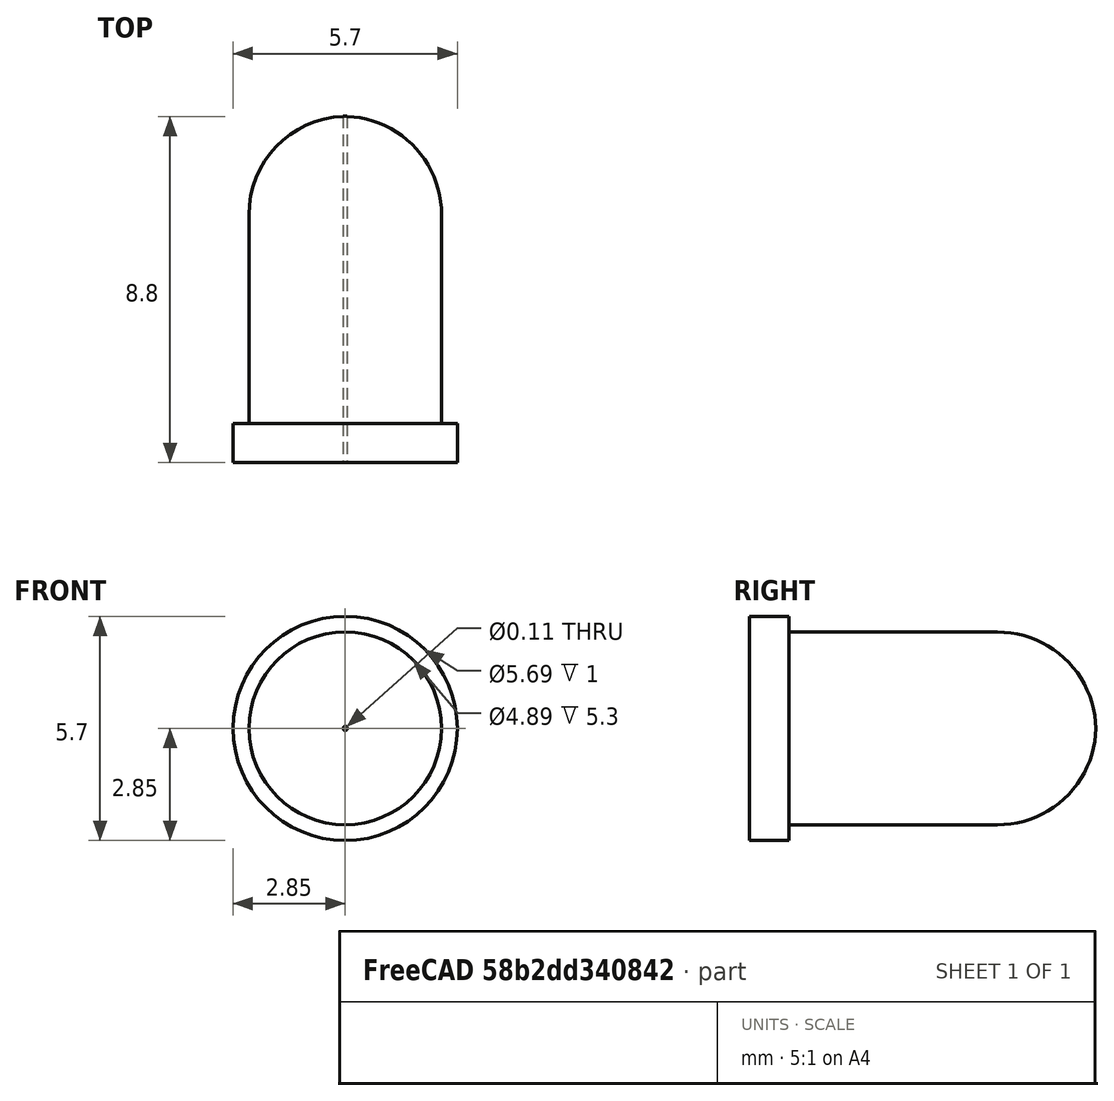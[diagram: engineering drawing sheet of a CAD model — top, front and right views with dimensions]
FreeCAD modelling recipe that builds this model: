
FCSTD DOCUMENT
Label: 5mmLED
objects: Sketcher::SketchObject×1, Part::Revolution×1
note: 2 computed .brp shape members not serialized (recipe doc carries the construction recipe); baked Part::Feature solids carry a one-line shape summary decoded from their .brp

FEATURE [Sketcher::SketchObject] Sketch
  sketch-geometry (6):
    g0: LineSegment StartX=0.052514 StartY=51.5718 StartZ=0 EndX=0.052514 EndY=42.7718 EndZ=0
    g1: LineSegment StartX=0.052514 StartY=42.7718 StartZ=0 EndX=-2.84749 EndY=42.7718 EndZ=0
    g2: LineSegment StartX=-2.84749 StartY=42.7718 StartZ=0 EndX=-2.84749 EndY=43.7718 EndZ=0
    g3: LineSegment StartX=-2.84749 StartY=43.7718 StartZ=0 EndX=-2.44749 EndY=43.7718 EndZ=0
    g4: LineSegment StartX=-2.44749 StartY=43.7718 StartZ=0 EndX=-2.44749 EndY=49.0718 EndZ=0
    g5: ArcOfCircle CenterX=0.052514 CenterY=49.0718 CenterZ=0 NormalX=0 NormalY=0 NormalZ=1 Radius=2.5 StartAngle=1.5708 EndAngle=3.14159
  constraints (17):
    c: Coincident(g0,g1)
    c: Coincident(g1,g2)
    c: Coincident(g2,g3)
    c: Coincident(g3,g4)
    c: Coincident(g5,g0)
    c: Coincident(g5,g4)
    c: Parallel(g4,g0)
    c: Parallel(g3,g1)
    c: Parallel(g2,g0)
    c: Distance(g0) = 8.8
    c: Distance(g1) = 2.9
    c: Distance(g2) = 1
    c: Perpendicular(g1,g0)
    c: Radius(g5) = 2.5
    c: PointOnObject(g5,g0)
    c: Horizontal(g1)
    c: Distance(g4) = 5.3
FEATURE [Part::Revolution] Revolve
  Angle = 360
  Axis = (0,1,0)
  Base = (0,0,0)
  Source = -> Sketch
